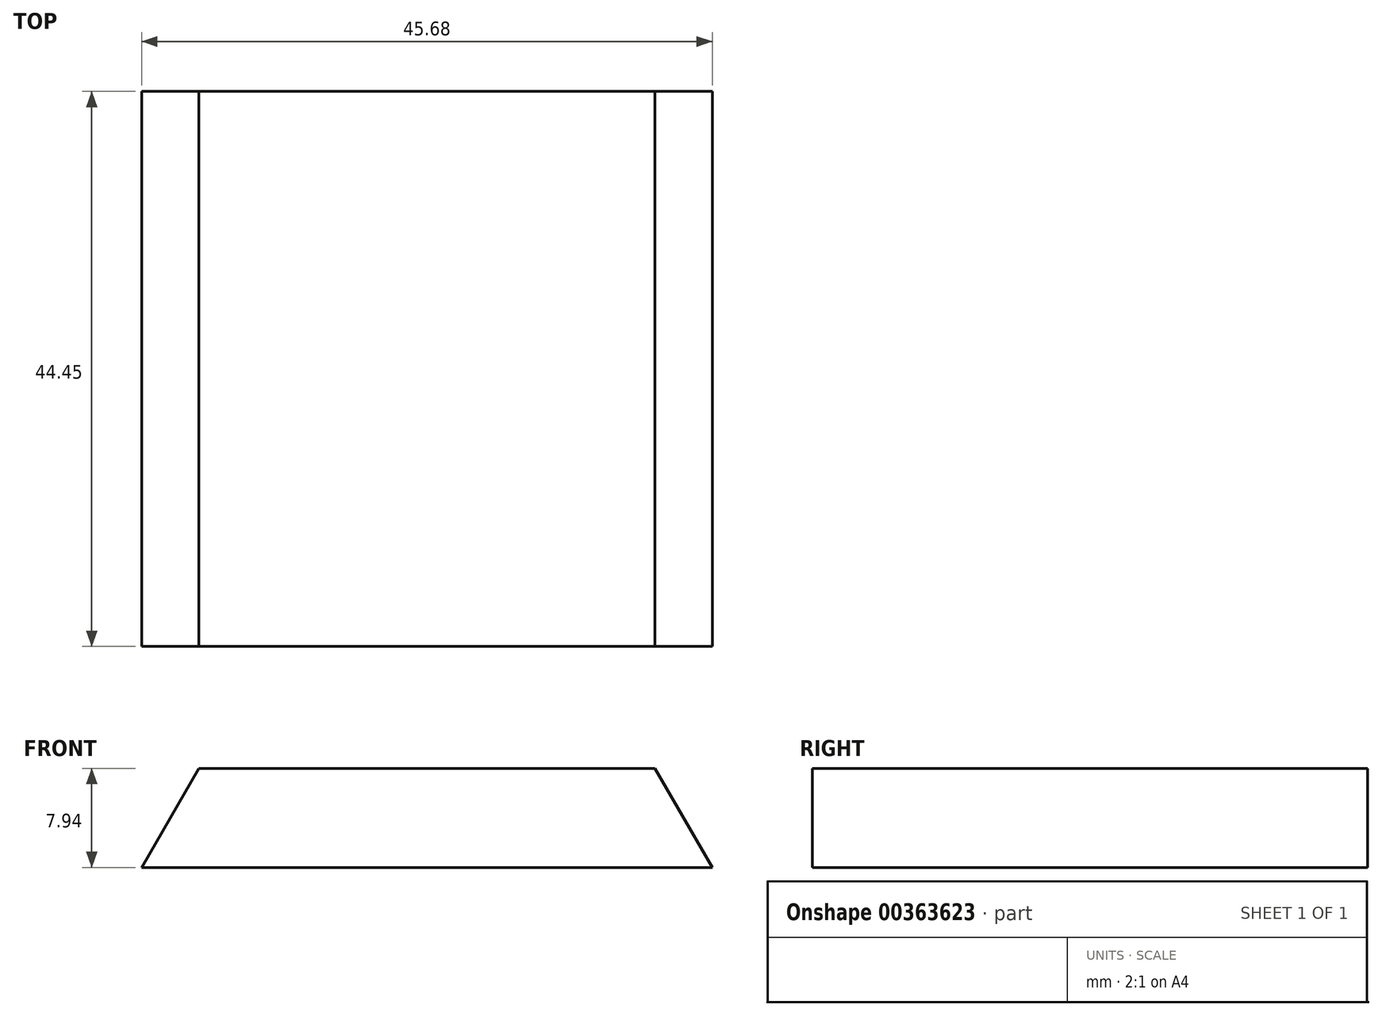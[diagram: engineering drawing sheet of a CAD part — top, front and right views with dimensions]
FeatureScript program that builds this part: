
annotation { "Feature Type Name" : "Feature", "Feature Type Description" : "" }
export const myFeature = defineFeature(function(context is Context, id is Id, definition is map)
    precondition{}
    {
        {
            var Q0;
            Q0=qCreatedBy(makeId("Top.planeOp"),FACE);
            var sketch = newSketch(context, id + "F0", { "sketchPlane" : qUnion([Q0])});
            skLineSegment(sketch, "E0.bottom", {"start": v(-19.2, 39.34) * mm, "end": v(26.83, 39.34) * mm});
            skLineSegment(sketch, "E0.top", {"start": v(-19.2, -5.1) * mm, "end": v(26.83, -5.1) * mm});
            skLineSegment(sketch, "E0.left", {"start": v(-19.2, 39.34) * mm, "end": v(-19.2, -5.1) * mm});
            skLineSegment(sketch, "E0.right", {"start": v(26.83, 39.34) * mm, "end": v(26.83, -5.1) * mm});
            skSolve(sketch);
        }
        {
            var Q0;
            Q0=qSketchRegion(id+"F0",true);
            extrude(context, id + "F1", {"entities" : qUnion([Q0]), "depth" : 7.94 * mm});
        }
        {
            var Q0;
            Q0=makeQuery(id+"F1.opExtrude","CAP_EDGE",EDGE,{"disambiguationData":[OSD([sQuery(id+"F0.wireOp",EDGE,"E0.left")])],"isStart":false});
            var Q1;
            Q1=makeQuery(id+"F1.opExtrude","CAP_EDGE",EDGE,{"disambiguationData":[OSD([sQuery(id+"F0.wireOp",EDGE,"E0.right")])],"isStart":false});
            chamfer(context, id + "F2", {"entities" : qUnion([Q0, Q1]), "chamferType" : ChamferType.OFFSET_ANGLE, "width" : 4.76 * mm, "oppositeDirection" : false, "angle" : 60 * degree, "tangentPropagation" : true});
        }
    });
